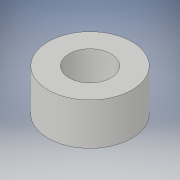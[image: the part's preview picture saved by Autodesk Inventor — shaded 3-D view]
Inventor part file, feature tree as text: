
AUTODESK INVENTOR PART (.ipt)
format: ipt  version: 2018 (Build 220112000, 112)  size: 94,720 bytes
history: native  units: in
note: dims shown in document units (in); Inventor stores cm internally (conversion verified against a paired STEP export)
features: extrude x1, sketch x1
ambient origin geometry x8: Origin, YZ Plane, XZ Plane, XY Plane, X Axis, Y Axis, Z Axis, Center Point
bodies: Solid1 (feature_tree)
feature tree (2):
  extrude  "Extrusion1"  Depth=0.1181in
  sketch  "Sketch1"  dims[d0=0.1181in d1=0.2362in d2=0.1181in d3=0.0in]
